# Revit family: QF_Vivreau_PURITY C1100 XtraSafe
name_source: partatom
category: Specialty Equipment
units: mm (PartAtom-declared; Revit-internal decimal feet)

## family parameters
Always vertical = Yes
Cut with Voids When Loaded = No
OmniClass Number = 23.40.40.14.24
OmniClass Title = Food Dispensing Equipment
Part Type = Normal
Room Calculation Point = No
Round Connector Dimension = Use Diameter
Shared = No
Work Plane-Based = No

## types (1)
- QF_Vivreau_PURITY C1100 XtraSafe
    Assembly Code = E1090320
    CSI MasterFormat = 11 46 00
    Cold Water Connection Height = 1' - 9"
    Cold Water Flow = 26.410 gal/h
    Cold Water Maximum Pressure = 125.00 psi
    Cold Water Minimum Pressure = 29.00 psi
    Cold Water RI Height = 0' - 0"
    Cold Water Size = 1"
    Cold Water Temperature Recommended = 40 °F
    Depth = 0' - 7 1/4"
    Description = Water Filter
    Foodservice Equipment Identifier = Yes
    Height = 1' - 9 19/32"
    Identify Quantity as Lot = Yes
    Manufacturer = Vivreau
    Masterspec = Division 11
    Model = PURITY C1100 XtraSafe
    Plumbing Connection Type = NPT
    Specification by Manufacturer = PURITY C1100 XtraSafe water filtration cartridge. Calculate user-specific recommendations for capacity and filtration bypass settings for Coffee and Steam applications on VIVREAU website. Max. operating pressure 125 psi, water intake temperature 39-86 degrees Fahrenheit. Nominal flow 100 l/h (pressure loss at nominal flow 2.9 psi). Dimensions w/d/h with filter head 7.24/7.24/21.6 inch, weight dry/wet 16.9/27.5 lbs, position vertical. Technology complete desalination. Five step filtration process with pre-filtration, cation reduction, anion reduction, activated carbon filtration and fine filtration to protect against chlorides, sulphates and gypsum deposits.
    URL = www.vivreauwater.com/Professional-filters
    URL Cutsheet = https://vivreauwater.com
    Weight in Pounds = 16.9
    Width = 0' - 7 1/4"

## geometry (parser evidence)
native form markers: Sweep x7
no freeform markers — native parametric forms only
